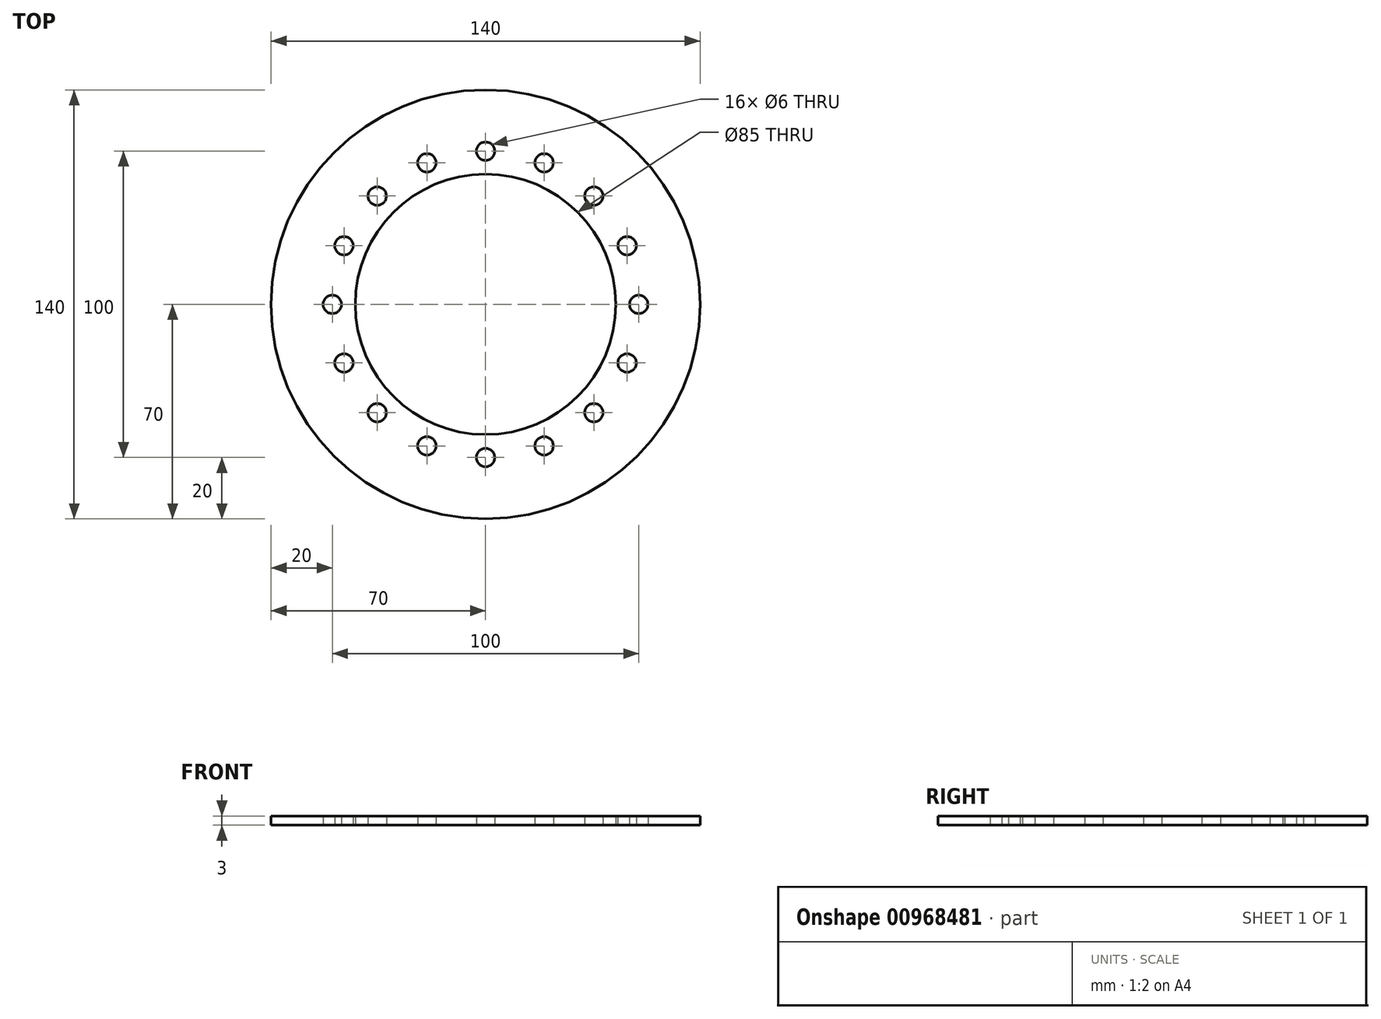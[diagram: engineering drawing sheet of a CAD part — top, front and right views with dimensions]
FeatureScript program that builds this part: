
annotation { "Feature Type Name" : "Feature", "Feature Type Description" : "" }
export const myFeature = defineFeature(function(context is Context, id is Id, definition is map)
    precondition{}
    {
        {
            var Q0;
            Q0=qCreatedBy(makeId("Top.planeOp"),FACE);
            var sketch = newSketch(context, id + "F0", { "sketchPlane" : qUnion([Q0])});
            skCircle(sketch, "E0", {"center": v(0, 0) * mm, "radius": 70 * mm});
            skCircle(sketch, "E1", {"center": v(0, 0) * mm, "radius": 50 * mm, "construction": true});
            skCircle(sketch, "E2", {"center": v(0, 50) * mm, "radius": 3 * mm});
            skCircle(sketch, "E3.1.0", {"center": v(-19.13, 46.2) * mm, "radius": 3 * mm});
            skCircle(sketch, "E3.2.0", {"center": v(-35.36, 35.36) * mm, "radius": 3 * mm});
            skCircle(sketch, "E3.3.0", {"center": v(-46.2, 19.13) * mm, "radius": 3 * mm});
            skCircle(sketch, "E3.4.0", {"center": v(-50, 0) * mm, "radius": 3 * mm});
            skCircle(sketch, "E3.5.0", {"center": v(-46.2, -19.13) * mm, "radius": 3 * mm});
            skCircle(sketch, "E3.6.0", {"center": v(-35.36, -35.36) * mm, "radius": 3 * mm});
            skCircle(sketch, "E3.7.0", {"center": v(-19.13, -46.2) * mm, "radius": 3 * mm});
            skCircle(sketch, "E3.8.0", {"center": v(0, -50) * mm, "radius": 3 * mm});
            skCircle(sketch, "E3.9.0", {"center": v(19.13, -46.2) * mm, "radius": 3 * mm});
            skCircle(sketch, "E3.10.0", {"center": v(35.36, -35.36) * mm, "radius": 3 * mm});
            skCircle(sketch, "E3.11.0", {"center": v(46.2, -19.13) * mm, "radius": 3 * mm});
            skCircle(sketch, "E3.12.0", {"center": v(50, 0) * mm, "radius": 3 * mm});
            skCircle(sketch, "E3.13.0", {"center": v(46.2, 19.13) * mm, "radius": 3 * mm});
            skCircle(sketch, "E3.14.0", {"center": v(35.36, 35.36) * mm, "radius": 3 * mm});
            skCircle(sketch, "E3.15.0", {"center": v(19.13, 46.2) * mm, "radius": 3 * mm});
            skCircle(sketch, "E4", {"center": v(0, 0) * mm, "radius": 42.5 * mm});
            skSolve(sketch);
        }
        {
            var Q0;
            Q0 = qSketchRegion(id + "F0", true);
            extrude(context, id + "F1", {"entities" : qUnion([Q0]), "depth" : 3 * mm, "offsetDistance" : 25 * mm});
        }
    });
